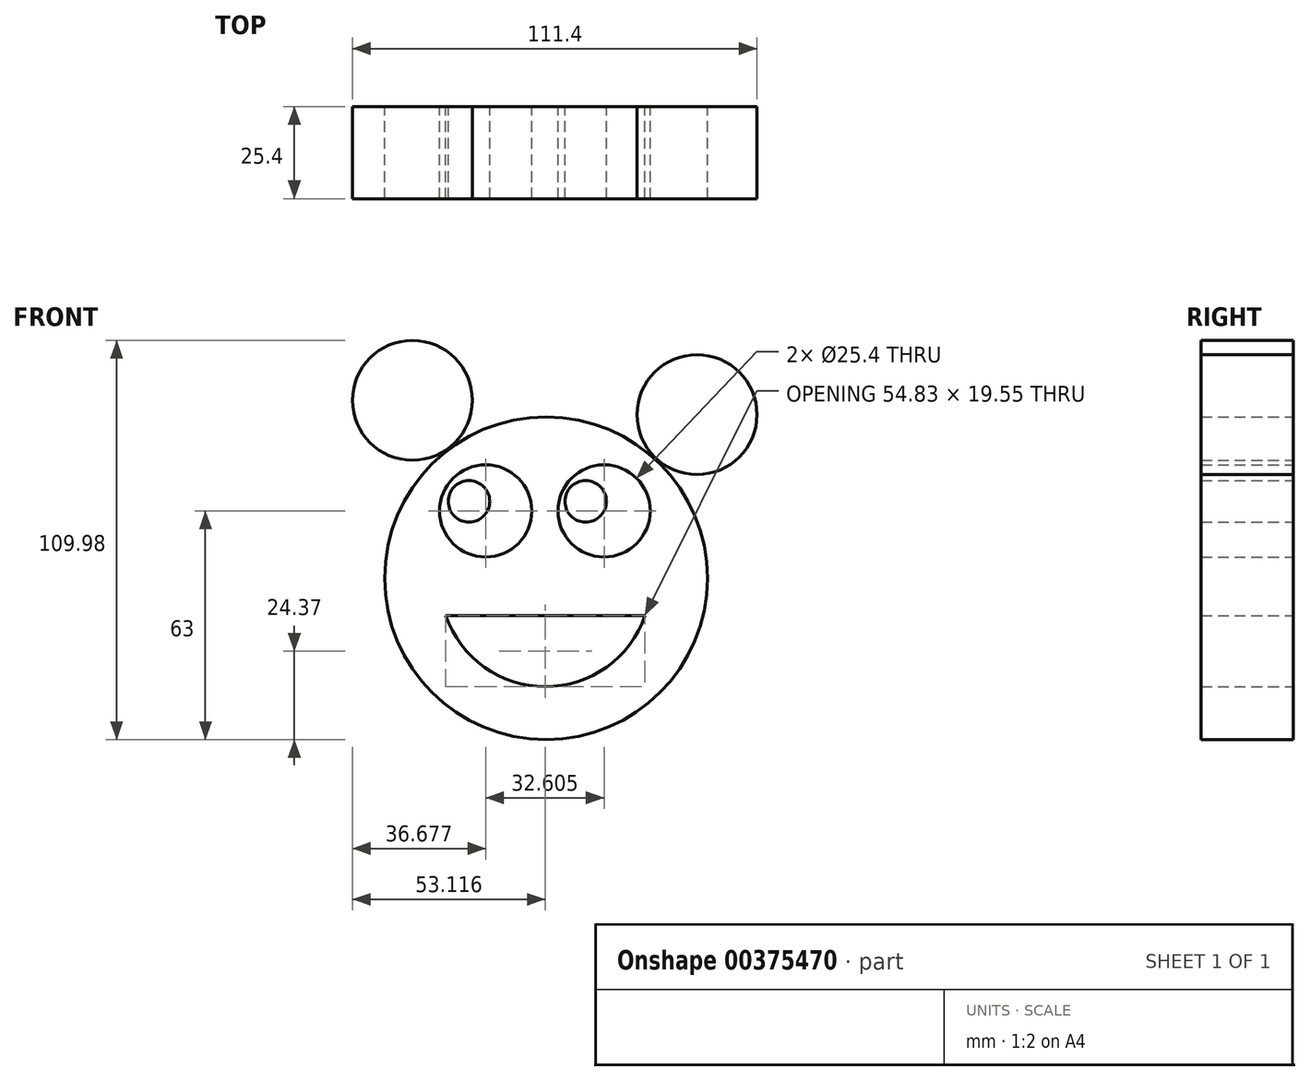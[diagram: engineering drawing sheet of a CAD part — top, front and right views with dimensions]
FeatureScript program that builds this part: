
annotation { "Feature Type Name" : "Feature", "Feature Type Description" : "" }
export const myFeature = defineFeature(function(context is Context, id is Id, definition is map)
    precondition{}
    {
        {
            var Q0;
            Q0=qCreatedBy(makeId("Front.planeOp"),FACE);
            var sketch = newSketch(context, id + "F0", { "sketchPlane" : qUnion([Q0])});
            skCircle(sketch, "E0", {"center": v(-36.8, 49.02) * mm, "radius": 16.51 * mm});
            skCircle(sketch, "E1", {"center": v(0, 0) * mm, "radius": 44.45 * mm});
            skCircle(sketch, "E2", {"center": v(41.59, 45.08) * mm, "radius": 16.51 * mm});
            skCircle(sketch, "E3", {"center": v(-16.62, 18.55) * mm, "radius": 12.7 * mm});
            skCircle(sketch, "E4", {"center": v(15.98, 18.55) * mm, "radius": 12.7 * mm});
            skLineSegment(sketch, "E5", {"start": v(-27.6, -10.3) * mm, "end": v(27.23, -10.3) * mm});
            skArc(sketch, "E6", {"start": v(-27.6, -10.3) * mm, "mid": v(-0.18, -29.86) * mm, "end": v(27.23, -10.3) * mm});
            skCircle(sketch, "E7", {"center": v(-21.23, 21.18) * mm, "radius": 5.72 * mm});
            skCircle(sketch, "E8", {"center": v(10.9, 21.18) * mm, "radius": 5.72 * mm});
            skSolve(sketch);
        }
        {
            var Q0;
            Q0=makeQuery(id+"F0.imprint","IMPRINT",FACE,{"disambiguationData":[TD([[makeQuery(id+"F0.imprint","IMPRINT",EDGE,{"derivedFrom":sQuery(id+"F0.wireOp",EDGE,"E2")}),1.0]])]});
            var Q1;
            Q1=makeQuery(id+"F0.imprint","IMPRINT",FACE,{"disambiguationData":[TD([[makeQuery(id+"F0.imprint","IMPRINT",EDGE,{"derivedFrom":sQuery(id+"F0.wireOp",EDGE,"E0")}),1.0]])]});
            var Q2;
            Q2=makeQuery(id+"F0.imprint","IMPRINT",FACE,{"disambiguationData":[TD([[makeQuery(id+"F0.imprint","IMPRINT",EDGE,{"derivedFrom":sQuery(id+"F0.wireOp",EDGE,"E1")}),1.0]])]});
            var Q3;
            Q3=makeQuery(id+"F0.imprint","IMPRINT",FACE,{"disambiguationData":[TD([[makeQuery(id+"F0.imprint","IMPRINT",EDGE,{"derivedFrom":sQuery(id+"F0.wireOp",EDGE,"E7")}),1.0]])]});
            var Q4;
            Q4=makeQuery(id+"F0.imprint","IMPRINT",FACE,{"disambiguationData":[TD([[makeQuery(id+"F0.imprint","IMPRINT",EDGE,{"derivedFrom":sQuery(id+"F0.wireOp",EDGE,"E8")}),1.0]])]});
            extrude(context, id + "F1", {"entities" : qUnion([Q0, Q1, Q2, Q3, Q4]), "depth" : 25.4 * mm});
        }
    });
